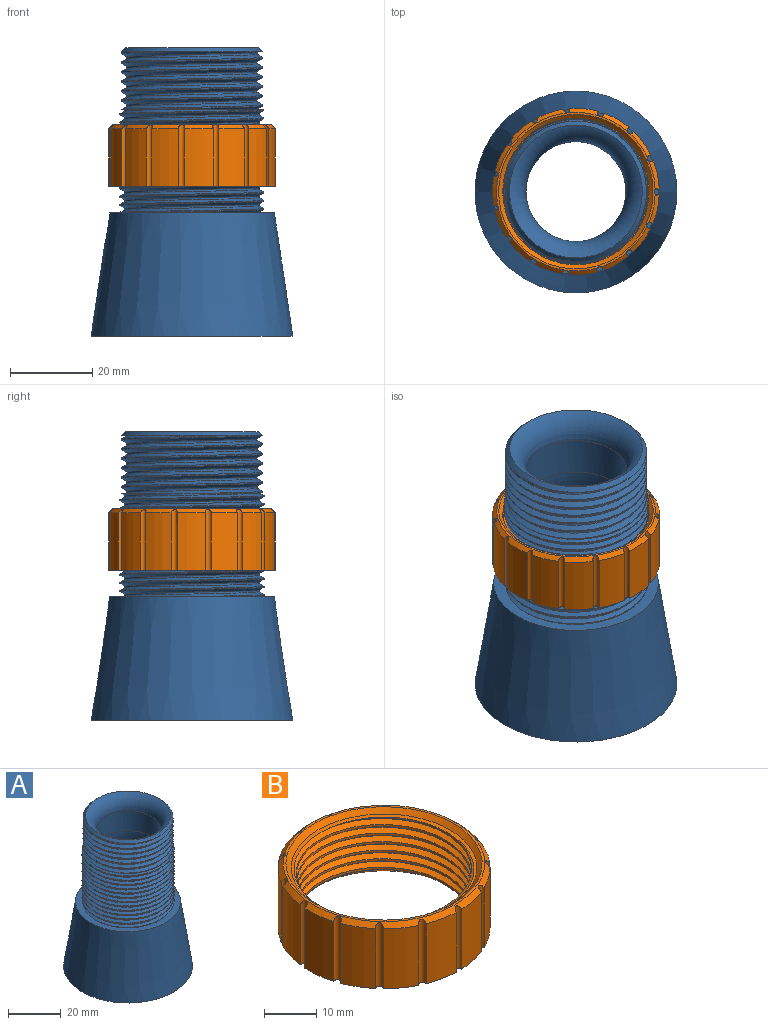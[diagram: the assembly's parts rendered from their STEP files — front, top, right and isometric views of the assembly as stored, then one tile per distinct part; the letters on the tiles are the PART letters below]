
ASSEMBLY  parts=2 mates=1
PART A: 22 faces, bbox 59.9x59.9x72.9 mm
  f0: plane 28.36x17.15mm, normal (0,0,-1), area 21.7mm2, adj f6,f14,f15,f16,f18,f19
  f1: plane 40.61x40.61mm, normal (0,0,1), area 361.7mm2, adj f3,f4,f14,f15,f16
  f2: plane 49x49mm, normal (0,0,-1), area 113.7mm2, adj f3,f13
  f3: cone r=20mm half-angle=8.5deg, axis (0,0,-1), area 4240.9mm2, adj f1,f2
  f4: cylinder r=17.5mm len=35mm, axis (0,0,-1), area 282.7mm2, adj f1,f5,f15,f16
  f5: plane 34.25x30.02mm, normal (0,0,1), area 71.3mm2, adj f4,f15,f16,f17,f18,f19
  f6: cylinder r=17.12mm len=34.24mm, axis (0,0,-1), area 199.3mm2, adj f0,f10,f18,f19
  f7: cone r=15.06mm half-angle=8.5deg, axis (0,0,-1), area 2273.2mm2, adj f11,f13
  f8: cylinder r=12.5mm len=25mm, axis (0,0,-1), area 1003.2mm2, adj f11,f12
  f9: cylinder r=12.12mm len=24.24mm, axis (0,0,-1), area 710.7mm2, adj f12,f21
  f10: cone r=16.12mm half-angle=45deg, axis (0,0,-1), area 147.7mm2, adj f6,f20,f21
  f11: torus R=37.5mm, axis (0,0,-1), area 1089.6mm2, adj f7,f8
  f12: torus R=37.12mm, axis (0,0,-1), area 335.8mm2, adj f8,f9
  f13: torus R=23.75mm, axis (0,0,1), area 927.1mm2, adj f2,f7
  f14: bspline ~37.91x32.84mm, area 718.1mm2, adj f0,f1,f15,f16
  f15: bspline ~40.41x35mm, area 1667.3mm2, adj f0,f1,f4,f5,f14
  f16: bspline ~40.41x35mm, area 1666.4mm2, adj f0,f1,f4,f5,f14
  f17: bspline ~36.65x31.74mm, area 389.2mm2, adj f5,f18,f19,f20
  f18: bspline ~39.54x34.24mm, area 906.4mm2, adj f0,f5,f6,f17,f20
  f19: bspline ~39.54x34.24mm, area 907.5mm2, adj f0,f5,f6,f17,f20
  f20: plane 35.06x35.06mm, normal (0,0,-1), area 75.5mm2, adj f10,f17,f18,f19
  f21: torus R=19.12mm, axis (0,0,1), area 670.3mm2, adj f9,f10
PART B: 50 faces, bbox 40.8x41.7x15.3 mm
  f0: cylinder r=20.25mm len=14mm, axis (0,0,-1), area 96.3mm2, adj f15,f16,f27,f41
  f1: cylinder r=20.25mm len=14mm, axis (0,0,-1), area 96.3mm2, adj f15,f16,f40,f41
  f2: cylinder r=20.25mm len=14mm, axis (0,0,-1), area 96.6mm2, adj f15,f16,f39,f40
  f3: cylinder r=20.25mm len=14mm, axis (0,0,-1), area 97.3mm2, adj f15,f16,f38,f39
  f4: cylinder r=20.25mm len=14mm, axis (0,0,-1), area 98.5mm2, adj f15,f16,f37,f38
  f5: cylinder r=20.25mm len=14mm, axis (0,0,-1), area 100.2mm2, adj f15,f17,f36,f37
  f6: cylinder r=20.25mm len=14mm, axis (0,0,-1), area 102.1mm2, adj f15,f18,f35,f36
  f7: cylinder r=20.25mm len=14mm, axis (0,0,-1), area 103.6mm2, adj f15,f19,f34,f35
  f8: cylinder r=20.25mm len=14mm, axis (0,0,-1), area 104.3mm2, adj f15,f20,f33,f34
  f9: cylinder r=20.25mm len=14mm, axis (0,0,-1), area 103.6mm2, adj f15,f21,f32,f33
  f10: cylinder r=20.25mm len=14mm, axis (0,0,-1), area 102.1mm2, adj f15,f22,f31,f32
  f11: cylinder r=20.25mm len=14mm, axis (0,0,-1), area 100.2mm2, adj f15,f23,f30,f31
  f12: cylinder r=20.25mm len=14mm, axis (0,0,-1), area 98.5mm2, adj f15,f16,f29,f30
  f13: cylinder r=20.25mm len=14mm, axis (0,0,-1), area 97.3mm2, adj f15,f16,f28,f29
  f14: cylinder r=20.25mm len=14mm, axis (0,0,-1), area 96.6mm2, adj f15,f16,f27,f28
  f15: plane 40.5x40.49mm, normal (0,0,-1), area 165.3mm2, adj f0,f1,f2,f3,f4,f5,f6,f7
  f16: cone r=19.25mm half-angle=45deg, axis (0,0,-1), area 81.3mm2, adj f0,f1,f2,f3,f4,f12,f13,f14
  f17: cone r=19.25mm half-angle=45deg, axis (0,0,-1), area 9.9mm2, adj f5,f24,f36,f37
  f18: cone r=19.25mm half-angle=45deg, axis (0,0,-1), area 9.9mm2, adj f6,f24,f35,f36
  f19: cone r=19.25mm half-angle=45deg, axis (0,0,-1), area 9.9mm2, adj f7,f24,f34,f35
  f20: cone r=19.25mm half-angle=45deg, axis (0,0,-1), area 9.9mm2, adj f8,f24,f33,f34
  f21: cone r=19.25mm half-angle=45deg, axis (0,0,-1), area 9.9mm2, adj f9,f24,f32,f33
  f22: cone r=19.25mm half-angle=45deg, axis (0,0,-1), area 9.9mm2, adj f10,f24,f31,f32
  f23: cone r=19.25mm half-angle=45deg, axis (0,0,-1), area 9.9mm2, adj f11,f24,f30,f31
  f24: plane 38.5x38.5mm, normal (0,0,1), area 58.9mm2, adj f16,f17,f18,f19,f20,f21,f22,f23
  f25: cone r=18.75mm half-angle=45deg, axis (0,0,-1), area 162.2mm2, adj f15,f46,f47
  f26: cone r=17.75mm half-angle=45deg, axis (0,0,1), area 162.2mm2, adj f24,f45,f48
  f27: cylinder r=0.75mm len=14.77mm, axis (0,0,-1), area 34.4mm2, adj f0,f14,f15,f16
  f28: cylinder r=0.75mm len=14.83mm, axis (0,0,-1), area 36.2mm2, adj f13,f14,f15,f16
  f29: cylinder r=0.75mm len=14.92mm, axis (0,0,-1), area 39mm2, adj f12,f13,f15,f16
  f30: cylinder r=0.75mm len=15mm, axis (0,0,-1), area 42.1mm2, adj f11,f12,f15,f16,f23,f24
  f31: cylinder r=0.75mm len=15mm, axis (0,0,-1), area 45.6mm2, adj f10,f11,f15,f22,f23,f24
  f32: cylinder r=0.75mm len=15mm, axis (0,0,-1), area 48.4mm2, adj f9,f10,f15,f21,f22,f24
  f33: cylinder r=0.75mm len=15mm, axis (0,0,-1), area 50.1mm2, adj f8,f9,f15,f20,f21,f24
  f34: cylinder r=0.75mm len=15mm, axis (0,0,-1), area 50.1mm2, adj f7,f8,f15,f19,f20,f24
  f35: cylinder r=0.75mm len=15mm, axis (0,0,-1), area 48.4mm2, adj f6,f7,f15,f18,f19,f24
  f36: cylinder r=0.75mm len=15mm, axis (0,0,-1), area 45.6mm2, adj f5,f6,f15,f17,f18,f24
  f37: cylinder r=0.75mm len=15mm, axis (0,0,-1), area 42.1mm2, adj f4,f5,f15,f16,f17,f24
  f38: cylinder r=0.75mm len=14.92mm, axis (0,0,-1), area 39mm2, adj f3,f4,f15,f16
  f39: cylinder r=0.75mm len=14.83mm, axis (0,0,-1), area 36.2mm2, adj f2,f3,f15,f16
  f40: cylinder r=0.75mm len=14.77mm, axis (0,0,-1), area 34.4mm2, adj f1,f2,f15,f16
  f41: cylinder r=0.75mm len=14.75mm, axis (0,0,-1), area 33.7mm2, adj f0,f1,f15,f16
  f42: bspline ~41.18x35.67mm, area 887.9mm2, adj f44,f45,f46,f47,f48,f49
  f43: bspline ~41.18x35.67mm, area 878.3mm2, adj f44,f45,f46,f47,f48,f49
  f44: bspline ~41.39x35.85mm, area 212.5mm2, adj f42,f43,f45,f46
  f45: plane 13.37x13.13mm, normal (0,0,-1), area 2mm2, adj f26,f42,f43,f44
  f46: plane 13.37x13.13mm, normal (0,0,1), area 2mm2, adj f25,f42,f43,f44
  f47: plane 35.5x35.5mm, normal (0,0,-1), area 58.7mm2, adj f25,f42,f43,f49
  f48: plane 35.5x35.5mm, normal (0,0,1), area 58.7mm2, adj f26,f42,f43,f49
  f49: cylinder r=16.75mm len=33.5mm, axis (0,0,1), area 138.4mm2, adj f42,f43,f47,f48
PLACE A t=(-25.73,3.63,-8.02)mm fixed
PLACE B rot(axis=(0,0,-1),102.4deg) t=(-11.41,68.9,-1.64)mm
MATE cylindrical A.f4 <-> B.f0  axis (0,0,1) through (-25.73,3.63,-8.02)mm
